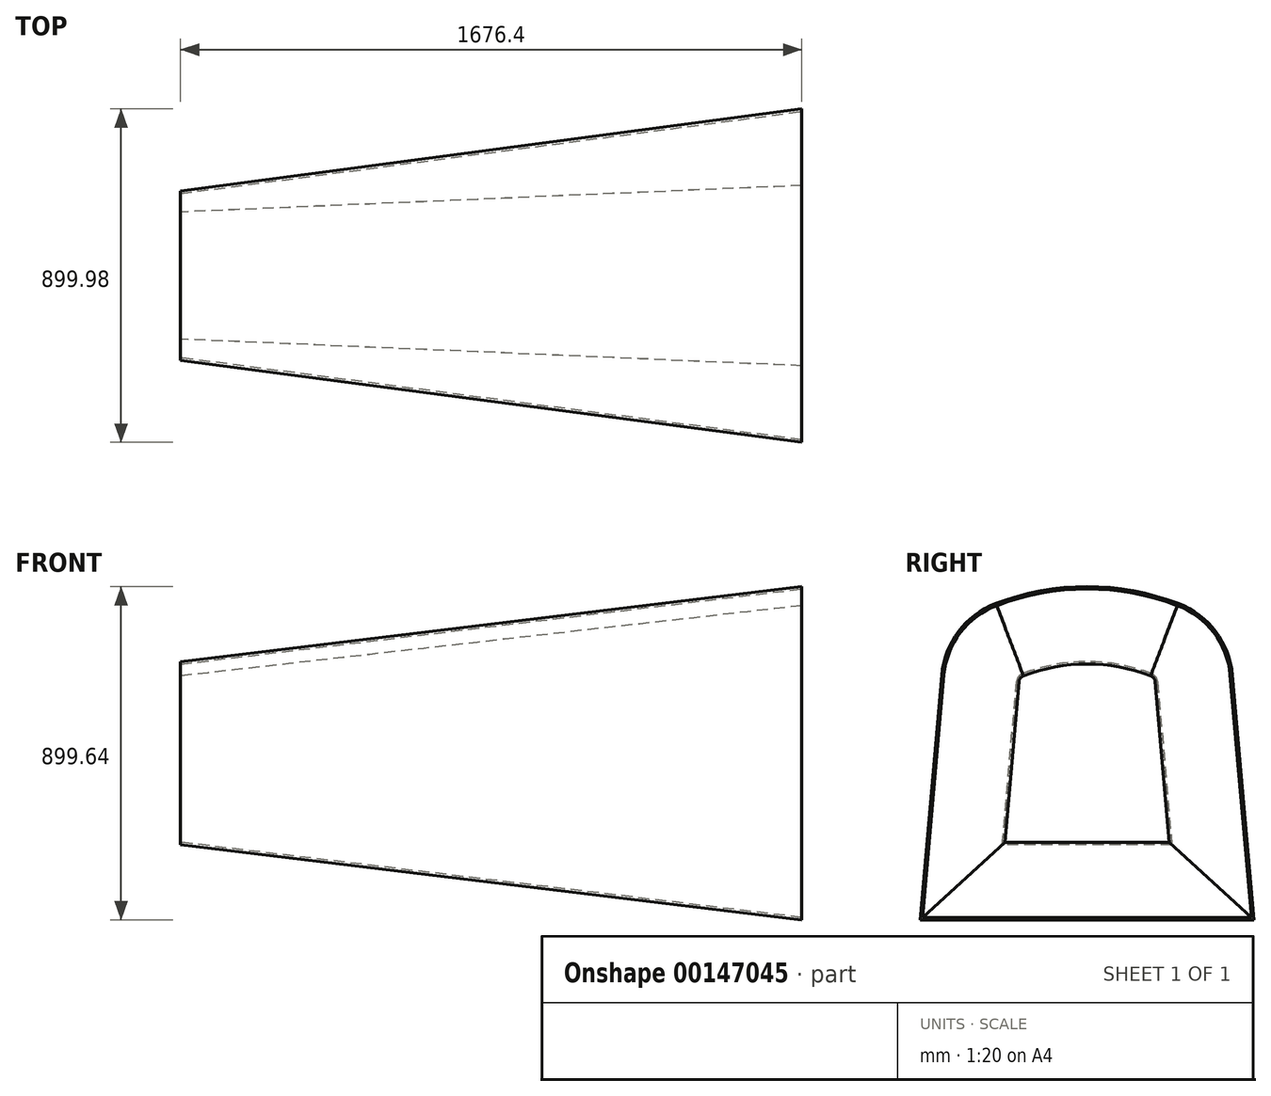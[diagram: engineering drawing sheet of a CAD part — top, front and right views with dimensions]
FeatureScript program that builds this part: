
annotation { "Feature Type Name" : "Feature", "Feature Type Description" : "" }
export const myFeature = defineFeature(function(context is Context, id is Id, definition is map)
    precondition{}
    {
        {
            var Q0;
            Q0=qCreatedBy(makeId("Right.planeOp"),FACE);
            var sketch = newSketch(context, id + "F0", { "sketchPlane" : qUnion([Q0])});
            skLineSegment(sketch, "E0", {"start": v(-228.6, 0) * mm, "end": v(-190.1, 439.98) * mm});
            skLineSegment(sketch, "E1", {"start": v(228.6, 0) * mm, "end": v(190.1, 439.98) * mm});
            skArc(sketch, "E2", {"start": v(173.96, 461.46) * mm, "mid": v(0, 493.9) * mm, "end": v(-173.96, 461.46) * mm});
            skLineSegment(sketch, "E3", {"start": v(-228.6, 0) * mm, "end": v(228.6, 0) * mm});
            skPoint(sketch, "E4.visualSharp", {"position": v(-188.75, 455.46) * mm});
            skArc(sketch, "E4.filletArc", {"start": v(-173.96, 461.46) * mm, "mid": v(-185.1, 453.03) * mm, "end": v(-190.1, 439.98) * mm});
            skPoint(sketch, "E5.visualSharp", {"position": v(188.75, 455.46) * mm});
            skArc(sketch, "E5.filletArc", {"start": v(190.1, 439.98) * mm, "mid": v(185.1, 453.03) * mm, "end": v(173.96, 461.46) * mm});
            skLineSegment(sketch, "E6", {"start": v(221.67, 6.35) * mm, "end": v(-221.67, 6.35) * mm});
            skLineSegment(sketch, "E7", {"start": v(221.67, 6.35) * mm, "end": v(183.73, 439.98) * mm});
            skLineSegment(sketch, "E8", {"start": v(-221.67, 6.35) * mm, "end": v(-183.73, 439.98) * mm});
            skArc(sketch, "E9.0", {"start": v(171.67, 455.54) * mm, "mid": v(0, 487.55) * mm, "end": v(-171.67, 455.54) * mm});
            skArc(sketch, "E10", {"start": v(183.73, 439.98) * mm, "mid": v(179.99, 449.53) * mm, "end": v(171.67, 455.54) * mm});
            skArc(sketch, "E11.MirrorCS", {"start": v(-183.73, 439.98) * mm, "mid": v(-179.99, 449.53) * mm, "end": v(-171.67, 455.54) * mm});
            skSolve(sketch);
        }
        {
            var Q0;
            Q0=makeQuery(id+"F0.imprint","IMPRINT",FACE,{"disambiguationData":[TD([[makeQuery(id+"F0.imprint","IMPRINT",EDGE,{"derivedFrom":sQuery(id+"F0.wireOp",EDGE,"E0")}),-1.0]])]});
            extrude(context, id + "F1", {"entities" : qUnion([Q0]), "depth" : 1676.4 * mm, "hasDraft" : true, "draftAngle" : 6.9 * degree});
        }
        {
            var Q0;
            Q0=makeQuery(id+"F0.imprint","IMPRINT",FACE,{"disambiguationData":[TD([[makeQuery(id+"F0.imprint","IMPRINT",EDGE,{"derivedFrom":sQuery(id+"F0.wireOp",EDGE,"E6")}),-1.0]])]});
            extrude(context, id + "F2", {"entities" : qUnion([Q0]), "operationType" : NewBodyOperationType.REMOVE, "depth" : 1676.4 * mm, "hasDraft" : true, "draftAngle" : 6.9 * degree});
        }
    });
